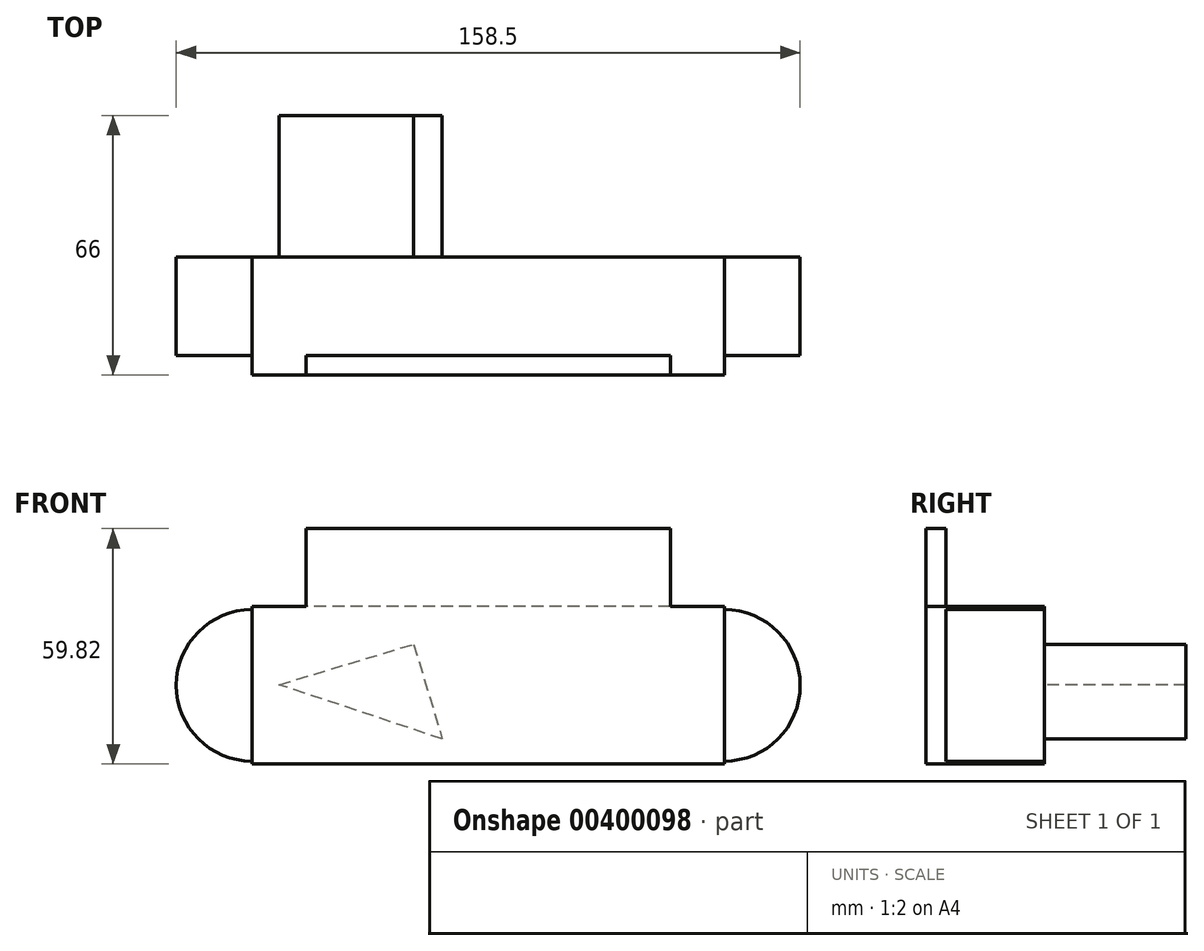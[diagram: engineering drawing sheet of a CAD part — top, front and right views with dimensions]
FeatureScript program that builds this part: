
annotation { "Feature Type Name" : "Feature", "Feature Type Description" : "" }
export const myFeature = defineFeature(function(context is Context, id is Id, definition is map)
    precondition{}
    {
        {
            var Q0;
            Q0=qCreatedBy(makeId("Front.planeOp"),FACE);
            var sketch = newSketch(context, id + "F0", { "sketchPlane" : qUnion([Q0])});
            skLineSegment(sketch, "E0.bottom", {"start": v(0, 0) * mm, "end": v(-46.24, 0) * mm});
            skLineSegment(sketch, "E0.top", {"start": v(0, 39.64) * mm, "end": v(-46.24, 39.64) * mm});
            skLineSegment(sketch, "E0.left", {"start": v(0, 0) * mm, "end": v(0, 39.64) * mm});
            skLineSegment(sketch, "E0.right", {"start": v(-46.24, 0) * mm, "end": v(-46.24, 39.64) * mm});
            skSolve(sketch);
        }
        {
            var Q0;
            Q0=makeQuery(id+"F0.imprint","IMPRINT",FACE,{"disambiguationData":[TD([[makeQuery(id+"F0.imprint","IMPRINT",EDGE,{"derivedFrom":sQuery(id+"F0.wireOp",EDGE,"E0.bottom")}),-1.0]])]});
            extrude(context, id + "F1", {"entities" : qUnion([Q0]), "depth" : 5 * mm});
        }
        {
            var Q0;
            Q0=makeQuery(id+"F1.opExtrude","CAP_FACE",FACE,{"disambiguationData":[OSD([sQuery(id+"F0.wireOp",EDGE,"E0.bottom"),sQuery(id+"F0.wireOp",EDGE,"E0.top"),sQuery(id+"F0.wireOp",EDGE,"E0.left"),sQuery(id+"F0.wireOp",EDGE,"E0.right")])],"isStart":false});
            var sketch = newSketch(context, id + "F2", { "sketchPlane" : qUnion([Q0])});
            skLineSegment(sketch, "E1.bottom", {"start": v(0, 19.82) * mm, "end": v(-60, 19.82) * mm});
            skLineSegment(sketch, "E1.top", {"start": v(0, -20.18) * mm, "end": v(-60, -20.18) * mm});
            skLineSegment(sketch, "E1.left", {"start": v(0, 19.82) * mm, "end": v(0, -20.18) * mm});
            skLineSegment(sketch, "E1.right", {"start": v(-60, 19.82) * mm, "end": v(-60, -20.18) * mm});
            skSolve(sketch);
        }
        {
            var Q0;
            Q0 = qSketchRegion(id + "F2", true);
            extrude(context, id + "F3", {"entities" : qUnion([Q0]), "operationType" : NewBodyOperationType.ADD, "oppositeDirection" : true, "depth" : 30 * mm});
        }
        {
            var Q0;
            Q0=makeQuery(id+"F3.opExtrude","CAP_FACE",FACE,{"disambiguationData":[OSD([sQuery(id+"F2.wireOp",EDGE,"E1.bottom"),sQuery(id+"F2.wireOp",EDGE,"E1.top"),sQuery(id+"F2.wireOp",EDGE,"E1.left"),sQuery(id+"F2.wireOp",EDGE,"E1.right")])],"isStart":false});
            var sketch = newSketch(context, id + "F4", { "sketchPlane" : qUnion([Q0])});
            skCircle(sketch, "E2", {"center": v(23.15, 0) * mm, "radius": 17.6 * mm});
            skCircle(sketch, "E3", {"center": v(60, -0.18) * mm, "radius": 19.25 * mm});
            skSolve(sketch);
        }
        {
            var Q0;
            {var subQ0=sQuery(id+"F4.wireOp",EDGE,"E3");var subQ1=makeQuery(id+"F3.opExtrude","CAP_EDGE",EDGE,{"disambiguationData":[OSD([sQuery(id+"F2.wireOp",EDGE,"E1.right")])],"isStart":false});var subQ2=makeQuery(id+"F4.imprint","INTERSECT",VERTEX,{"disambiguationData":[OD(0.0)],"derivedFrom":[subQ1,subQ0]});Q0=makeQuery(id+"F4.imprint","IMPRINT",FACE,{"disambiguationData":[TD([[makeQuery(id+"F4.imprint","IMPRINT",EDGE,{"disambiguationData":[TD([[subQ2,1.0]])],"derivedFrom":subQ0}),1.0]])]});}
            extrude(context, id + "F5", {"entities" : qUnion([Q0]), "operationType" : NewBodyOperationType.ADD, "oppositeDirection" : true, "depth" : 25 * mm});
        }
        {
            var Q0;
            Q0=makeQuery(id+"F1.opExtrude","SWEPT_BODY",BODY,{"disambiguationData":[OSD([sQuery(id+"F0.wireOp",EDGE,"E0.bottom"),sQuery(id+"F0.wireOp",EDGE,"E0.top"),sQuery(id+"F0.wireOp",EDGE,"E0.left"),sQuery(id+"F0.wireOp",EDGE,"E0.right")])]});
            var Q1;
            Q1=qCreatedBy(makeId("Right.planeOp"),FACE);
            mirror(context, id + "F6", {"operationType" : NewBodyOperationType.ADD, "entities" : qUnion([Q0]), "mirrorPlane" : qUnion([Q1])});
        }
        {
            var Q0;
            {var subQ0=sQuery(id+"F2.wireOp",EDGE,"E1.right");var subQ1=makeQuery(id+"F5.boolean.opBoolean","MERGE",FACE,{"derivedFrom":[makeQuery(id+"F3.opExtrude","CAP_FACE",FACE,{"disambiguationData":[OSD([sQuery(id+"F2.wireOp",EDGE,"E1.bottom"),sQuery(id+"F2.wireOp",EDGE,"E1.top"),sQuery(id+"F2.wireOp",EDGE,"E1.left"),subQ0])],"isStart":false}),makeQuery(id+"F5.opExtrude","CAP_FACE",FACE,{"disambiguationData":[OSD([subQ0,sQuery(id+"F4.wireOp",EDGE,"E3")])],"isStart":true})]});Q0=makeQuery(id+"F6.boolean.opBoolean","MERGE",FACE,{"derivedFrom":[subQ1,makeQuery(id+"F6.opPattern","COPY",FACE,{"derivedFrom":subQ1,"instanceName":"1"})]});}
            var sketch = newSketch(context, id + "F7", { "sketchPlane" : qUnion([Q0])});
            skLineSegment(sketch, "E4", {"start": v(53.08, 0) * mm, "end": v(18.91, 10.27) * mm});
            skLineSegment(sketch, "E5", {"start": v(18.91, 10.27) * mm, "end": v(11.67, -13.8) * mm});
            skLineSegment(sketch, "E6", {"start": v(11.67, -13.8) * mm, "end": v(53.08, 0) * mm});
            skSolve(sketch);
        }
        {
            var Q0;
            Q0 = qSketchRegion(id + "F7", true);
            extrude(context, id + "F8", {"entities" : qUnion([Q0]), "operationType" : NewBodyOperationType.ADD, "depth" : 36 * mm});
        }
    });
